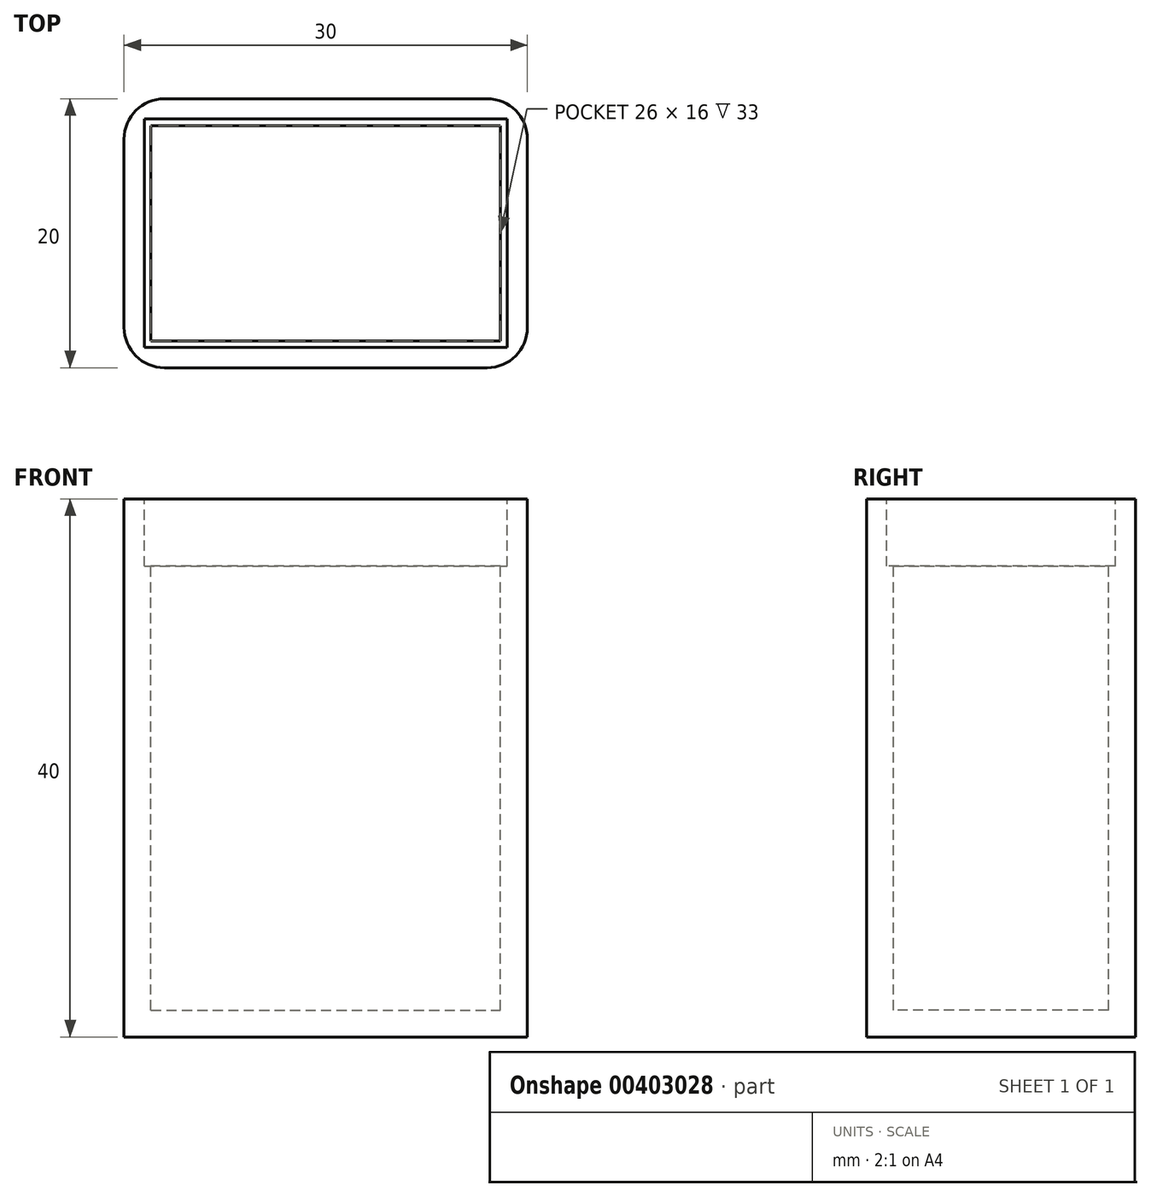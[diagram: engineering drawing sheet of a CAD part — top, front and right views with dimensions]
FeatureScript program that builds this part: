
annotation { "Feature Type Name" : "Feature", "Feature Type Description" : "" }
export const myFeature = defineFeature(function(context is Context, id is Id, definition is map)
    precondition{}
    {
        {
            var Q0;
            Q0=qCreatedBy(makeId("Top.planeOp"),FACE);
            var sketch = newSketch(context, id + "F0", { "sketchPlane" : qUnion([Q0])});
            skLineSegment(sketch, "E0.bottom", {"start": v(-20.63, 29.21) * mm, "end": v(9.37, 29.21) * mm});
            skLineSegment(sketch, "E0.top", {"start": v(-20.63, 9.21) * mm, "end": v(9.37, 9.21) * mm});
            skLineSegment(sketch, "E0.left", {"start": v(-20.63, 29.21) * mm, "end": v(-20.63, 9.21) * mm});
            skLineSegment(sketch, "E0.right", {"start": v(9.37, 29.21) * mm, "end": v(9.37, 9.21) * mm});
            skSolve(sketch);
        }
        {
            var Q0;
            Q0 = qSketchRegion(id + "F0", true);
            extrude(context, id + "F1", {"entities" : qUnion([Q0]), "depth" : 40 * mm});
        }
        {
            var Q0;
            Q0=makeQuery(id+"F1.opExtrude","CAP_FACE",FACE,{"disambiguationData":[OSD([sQuery(id+"F0.wireOp",EDGE,"E0.bottom"),sQuery(id+"F0.wireOp",EDGE,"E0.top"),sQuery(id+"F0.wireOp",EDGE,"E0.left"),sQuery(id+"F0.wireOp",EDGE,"E0.right")])],"isStart":false});
            var sketch = newSketch(context, id + "F2", { "sketchPlane" : qUnion([Q0])});
            skLineSegment(sketch, "E1.bottom", {"start": v(-18.63, 27.21) * mm, "end": v(7.37, 27.21) * mm});
            skLineSegment(sketch, "E1.top", {"start": v(-18.63, 11.21) * mm, "end": v(7.37, 11.21) * mm});
            skLineSegment(sketch, "E1.left", {"start": v(-18.63, 27.21) * mm, "end": v(-18.63, 11.21) * mm});
            skLineSegment(sketch, "E1.right", {"start": v(7.37, 27.21) * mm, "end": v(7.37, 11.21) * mm});
            skSolve(sketch);
        }
        {
            var Q0;
            Q0 = qSketchRegion(id + "F2", true);
            extrude(context, id + "F3", {"entities" : qUnion([Q0]), "operationType" : NewBodyOperationType.REMOVE, "oppositeDirection" : true, "depth" : 38 * mm});
        }
        {
            var Q0;
            Q0=makeQuery(id+"F1.opExtrude","CAP_FACE",FACE,{"disambiguationData":[OSD([sQuery(id+"F0.wireOp",EDGE,"E0.bottom"),sQuery(id+"F0.wireOp",EDGE,"E0.top"),sQuery(id+"F0.wireOp",EDGE,"E0.left"),sQuery(id+"F0.wireOp",EDGE,"E0.right")])],"isStart":false});
            var sketch = newSketch(context, id + "F4", { "sketchPlane" : qUnion([Q0])});
            skLineSegment(sketch, "E2.bottom", {"start": v(-19.13, 27.71) * mm, "end": v(7.87, 27.71) * mm});
            skLineSegment(sketch, "E2.top", {"start": v(-19.13, 10.71) * mm, "end": v(7.87, 10.71) * mm});
            skLineSegment(sketch, "E2.left", {"start": v(-19.13, 27.71) * mm, "end": v(-19.13, 10.71) * mm});
            skLineSegment(sketch, "E2.right", {"start": v(7.87, 27.71) * mm, "end": v(7.87, 10.71) * mm});
            skSolve(sketch);
        }
        {
            var Q0;
            Q0 = qSketchRegion(id + "F4", true);
            extrude(context, id + "F5", {"entities" : qUnion([Q0]), "operationType" : NewBodyOperationType.REMOVE, "oppositeDirection" : true, "depth" : 5 * mm});
        }
        {
            var Q0;
            Q0=makeQuery(id+"F1.opExtrude","SWEPT_EDGE",EDGE,{"disambiguationData":[OSD([sQuery(id+"F0.wireOp",EDGE,"E0.top"),sQuery(id+"F0.wireOp",EDGE,"E0.left")])]});
            var Q1;
            Q1=makeQuery(id+"F1.opExtrude","SWEPT_EDGE",EDGE,{"disambiguationData":[OSD([sQuery(id+"F0.wireOp",EDGE,"E0.bottom"),sQuery(id+"F0.wireOp",EDGE,"E0.left")])]});
            var Q2;
            Q2=makeQuery(id+"F1.opExtrude","SWEPT_EDGE",EDGE,{"disambiguationData":[OSD([sQuery(id+"F0.wireOp",EDGE,"E0.top"),sQuery(id+"F0.wireOp",EDGE,"E0.right")])]});
            var Q3;
            Q3=makeQuery(id+"F1.opExtrude","SWEPT_EDGE",EDGE,{"disambiguationData":[OSD([sQuery(id+"F0.wireOp",EDGE,"E0.bottom"),sQuery(id+"F0.wireOp",EDGE,"E0.right")])]});
            fillet(context, id + "F6", {"entities" : qUnion([Q0, Q1, Q2, Q3]), "radius" : 3 * mm, "tangentPropagation" : true, "allowEdgeOverflow" : false});
        }
    });
